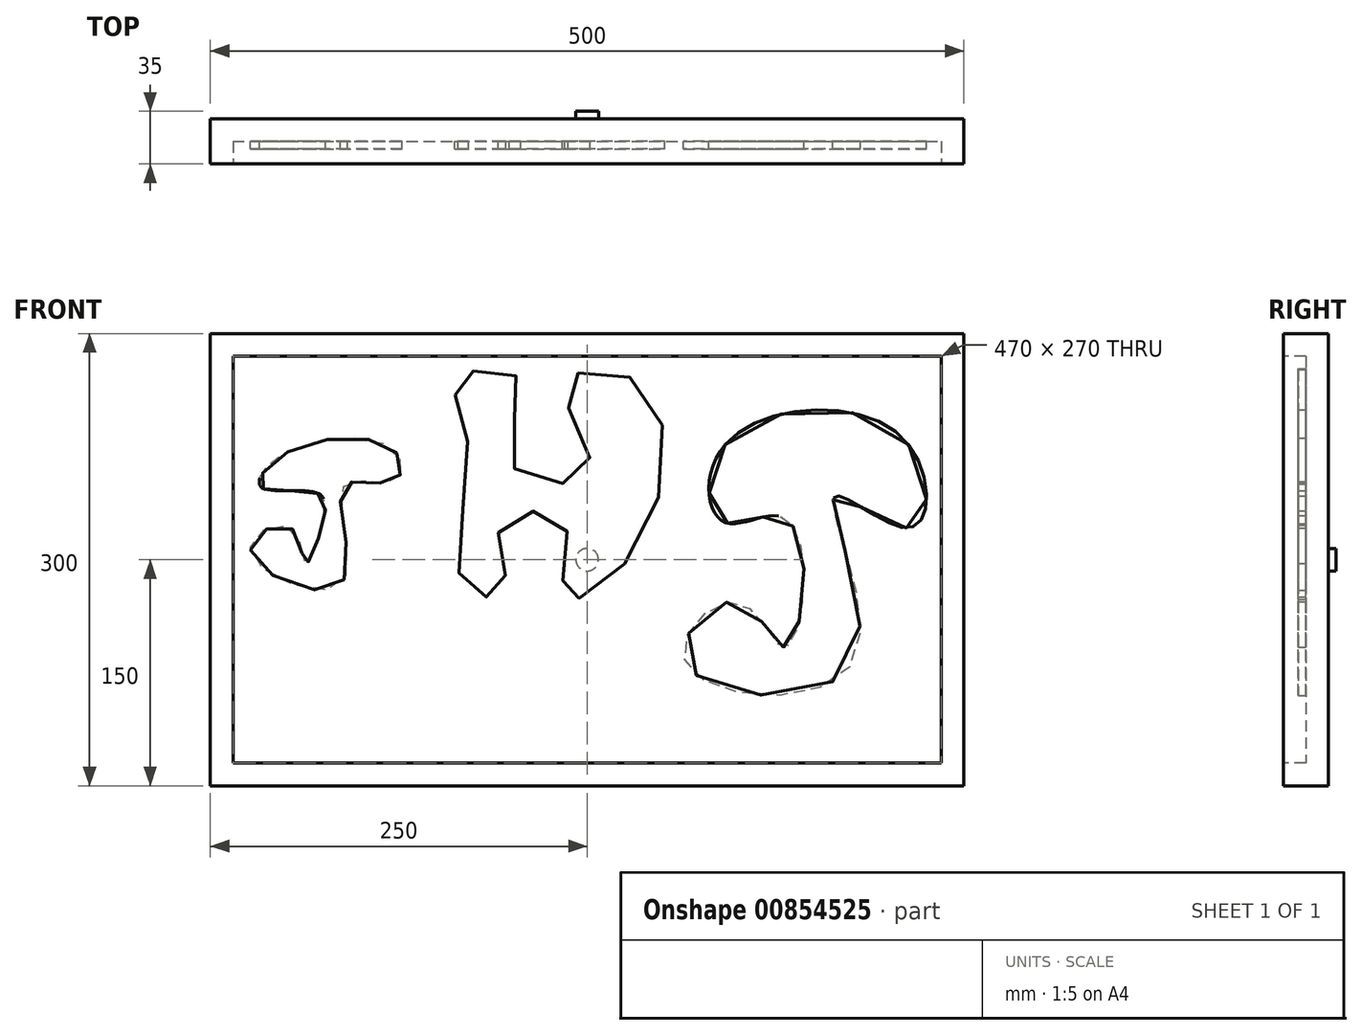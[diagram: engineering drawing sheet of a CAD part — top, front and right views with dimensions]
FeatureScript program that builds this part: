
annotation { "Feature Type Name" : "Feature", "Feature Type Description" : "" }
export const myFeature = defineFeature(function(context is Context, id is Id, definition is map)
    precondition{}
    {
        {
            var Q0;
            Q0=qCreatedBy(makeId("Front.planeOp"),FACE);
            var sketch = newSketch(context, id + "F0", { "sketchPlane" : qUnion([Q0])});
            skLineSegment(sketch, "E0.bottom", {"start": v(-500, 300) * mm, "end": v(0, 300) * mm});
            skLineSegment(sketch, "E0.top", {"start": v(-500, 0) * mm, "end": v(0, 0) * mm});
            skLineSegment(sketch, "E0.left", {"start": v(-500, 300) * mm, "end": v(-500, 0) * mm});
            skLineSegment(sketch, "E0.right", {"start": v(0, 300) * mm, "end": v(0, 0) * mm});
            skSolve(sketch);
        }
        {
            var Q0;
            Q0=makeQuery(id+"F0.imprint","IMPRINT",FACE,{"disambiguationData":[TD([[makeQuery(id+"F0.imprint","IMPRINT",EDGE,{"derivedFrom":sQuery(id+"F0.wireOp",EDGE,"E0.bottom")}),-1.0]])]});
            extrude(context, id + "F1", {"entities" : qUnion([Q0]), "depth" : 30 * mm, "offsetDistance" : 25 * mm});
        }
        {
            var Q0;
            Q0=makeQuery(id+"F1.opExtrude","CAP_FACE",FACE,{"disambiguationData":[OSD([sQuery(id+"F0.wireOp",EDGE,"E0.bottom"),sQuery(id+"F0.wireOp",EDGE,"E0.top"),sQuery(id+"F0.wireOp",EDGE,"E0.left"),sQuery(id+"F0.wireOp",EDGE,"E0.right")])],"isStart":false});
            var sketch = newSketch(context, id + "F2", { "sketchPlane" : qUnion([Q0])});
            skLineSegment(sketch, "E1.bottom", {"start": v(-485, 285) * mm, "end": v(-15, 285) * mm});
            skLineSegment(sketch, "E1.top", {"start": v(-485, 15) * mm, "end": v(-15, 15) * mm});
            skLineSegment(sketch, "E1.left", {"start": v(-485, 285) * mm, "end": v(-485, 15) * mm});
            skLineSegment(sketch, "E1.right", {"start": v(-15, 285) * mm, "end": v(-15, 15) * mm});
            skSolve(sketch);
        }
        {
            var Q0;
            Q0=makeQuery(id+"F2.imprint","IMPRINT",FACE,{"disambiguationData":[TD([[makeQuery(id+"F2.imprint","IMPRINT",EDGE,{"derivedFrom":sQuery(id+"F2.wireOp",EDGE,"E1.bottom")}),-1.0]])]});
            extrude(context, id + "F3", {"entities" : qUnion([Q0]), "operationType" : NewBodyOperationType.REMOVE, "oppositeDirection" : true, "depth" : 15 * mm, "offsetDistance" : 25 * mm});
        }
        {
            var Q0;
            Q0=makeQuery(id+"F3.boolean.opBoolean","COPY",FACE,{"derivedFrom":makeQuery(id+"F3.opExtrude","CAP_FACE",FACE,{"disambiguationData":[OSD([sQuery(id+"F2.wireOp",EDGE,"E1.bottom"),sQuery(id+"F2.wireOp",EDGE,"E1.top"),sQuery(id+"F2.wireOp",EDGE,"E1.left"),sQuery(id+"F2.wireOp",EDGE,"E1.right")])],"isStart":false})});
            var sketch = newSketch(context, id + "F4", { "sketchPlane" : qUnion([Q0])});
            skFitSpline(sketch, "E2", {"points": [v(-448.8, 221.54) * mm, v(-377.53, 221.97) * mm, v(-378.22, 201.92) * mm, v(-411.8, 198.42) * mm, v(-413.9, 133.38) * mm, v(-473.34, 155.76) * mm, v(-447.23, 171.61) * mm, v(-436.97, 147.6) * mm, v(-425.78, 172.55) * mm, v(-429.05, 194.23) * mm, v(-466.11, 197.96) * mm, v(-448.8, 221.54) * mm]});
            skFitSpline(sketch, "E3", {"points": [v(-329.22, 228.5) * mm, v(-330.87, 130.91) * mm, v(-304.82, 131.24) * mm, v(-307.46, 171.8) * mm, v(-265.92, 175.42) * mm, v(-265.26, 126.3) * mm, v(-218.44, 156.3) * mm, v(-214.49, 266.09) * mm, v(-264.6, 265.43) * mm, v(-249.1, 209.05) * mm, v(-299.22, 211.69) * mm, v(-295.92, 270.37) * mm, v(-335.48, 270.04) * mm, v(-329.22, 228.5) * mm]});
            skFitSpline(sketch, "E4", {"points": [v(-158.47, 226.38) * mm, v(-40.98, 231.04) * mm, v(-35.38, 171.36) * mm, v(-85.74, 191.88) * mm, v(-74.55, 80.9) * mm, v(-184.58, 81.84) * mm, v(-151.01, 121.94) * mm, v(-120.24, 92.1) * mm, v(-106.25, 132.2) * mm, v(-122.1, 178.82) * mm, v(-159.4, 175.1) * mm, v(-158.47, 226.38) * mm]});
            skSolve(sketch);
        }
        {
            var Q0;
            Q0=makeQuery(id+"F4.imprint","IMPRINT",FACE,{"disambiguationData":[TD([[makeQuery(id+"F4.imprint","IMPRINT",EDGE,{"derivedFrom":sQuery(id+"F4.wireOp",EDGE,"E2")}),-1.0]])]});
            var Q1;
            Q1=makeQuery(id+"F4.imprint","IMPRINT",FACE,{"disambiguationData":[TD([[makeQuery(id+"F4.imprint","IMPRINT",EDGE,{"derivedFrom":sQuery(id+"F4.wireOp",EDGE,"E3")}),1.0]])]});
            var Q2;
            Q2=makeQuery(id+"F4.imprint","IMPRINT",FACE,{"disambiguationData":[TD([[makeQuery(id+"F4.imprint","IMPRINT",EDGE,{"derivedFrom":sQuery(id+"F4.wireOp",EDGE,"E4")}),-1.0]])]});
            extrude(context, id + "F5", {"entities" : qUnion([Q0, Q1, Q2]), "operationType" : NewBodyOperationType.ADD, "depth" : 5 * mm, "offsetDistance" : 25 * mm});
        }
        {
            var Q0;
            Q0=makeQuery(id+"F1.opExtrude","CAP_FACE",FACE,{"disambiguationData":[OSD([sQuery(id+"F0.wireOp",EDGE,"E0.bottom"),sQuery(id+"F0.wireOp",EDGE,"E0.top"),sQuery(id+"F0.wireOp",EDGE,"E0.left"),sQuery(id+"F0.wireOp",EDGE,"E0.right")])],"isStart":true});
            var sketch = newSketch(context, id + "F6", { "sketchPlane" : qUnion([Q0])});
            skCircle(sketch, "E5", {"center": v(250, 150) * mm, "radius": 7.5 * mm});
            skSolve(sketch);
        }
        {
            var Q0;
            Q0 = qSketchRegion(id + "F6", true);
            extrude(context, id + "F7", {"entities" : qUnion([Q0]), "operationType" : NewBodyOperationType.ADD, "depth" : 5 * mm, "offsetDistance" : 25 * mm});
        }
    });
